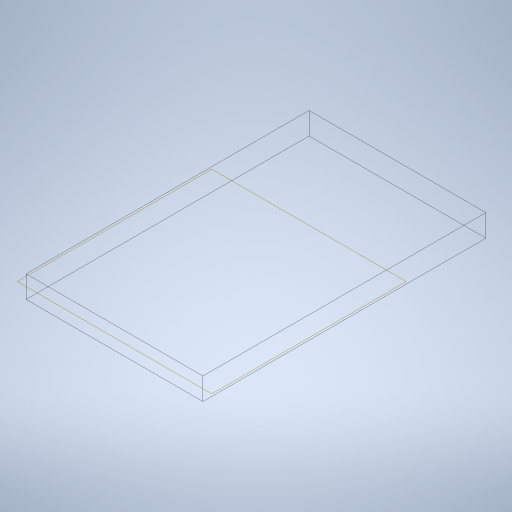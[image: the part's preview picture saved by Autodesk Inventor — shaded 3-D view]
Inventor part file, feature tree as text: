
AUTODESK INVENTOR PART (.ipt)
format: ipt  version: 2024.2 (Build 282272000, 272)  size: 296,960 bytes
history: native  units: in
note: dims shown in document units (in); Inventor stores cm internally (conversion verified against a paired STEP export)
features: sketch x5, extrude x3, plane x1, sweep x1
ambient origin geometry x8: Origin, YZ Plane, XZ Plane, XY Plane, X Axis, Y Axis, Z Axis, Center Point
bodies: Solid1 (feature_tree)
feature tree (10):
  extrude  "Extrusion1"  Depth=1.0in
  plane  "Work Plane1"
  sweep  "Sweep1"
  extrude  "Extrusion2"  Depth=0.1in
  extrude  "Extrusion3"  Depth=0.1in
  sketch  "Sketch1"  dims[d0=1.0in d1=1.5in]
  sketch  "Sketch2"  dims[d2=0.125in d3=0.0in d4=0.0625in]
  sketch  "Sketch4"  dims[d5=0.1in d6=0.1in]
  sketch  "Sketch5"  dims[d7=0.1in d8=0.1in]
  sketch  "Sketch6"  dims[d9=0.2in d10=0.2in d11=0.2in d12=0.875in d13=0.7627in d15=0.2in d16=0.1in d17=0.07in d18=0.0in d19=0.0in d20=0.05in d21=0.0in d22=0.05in d23=0.0in]
